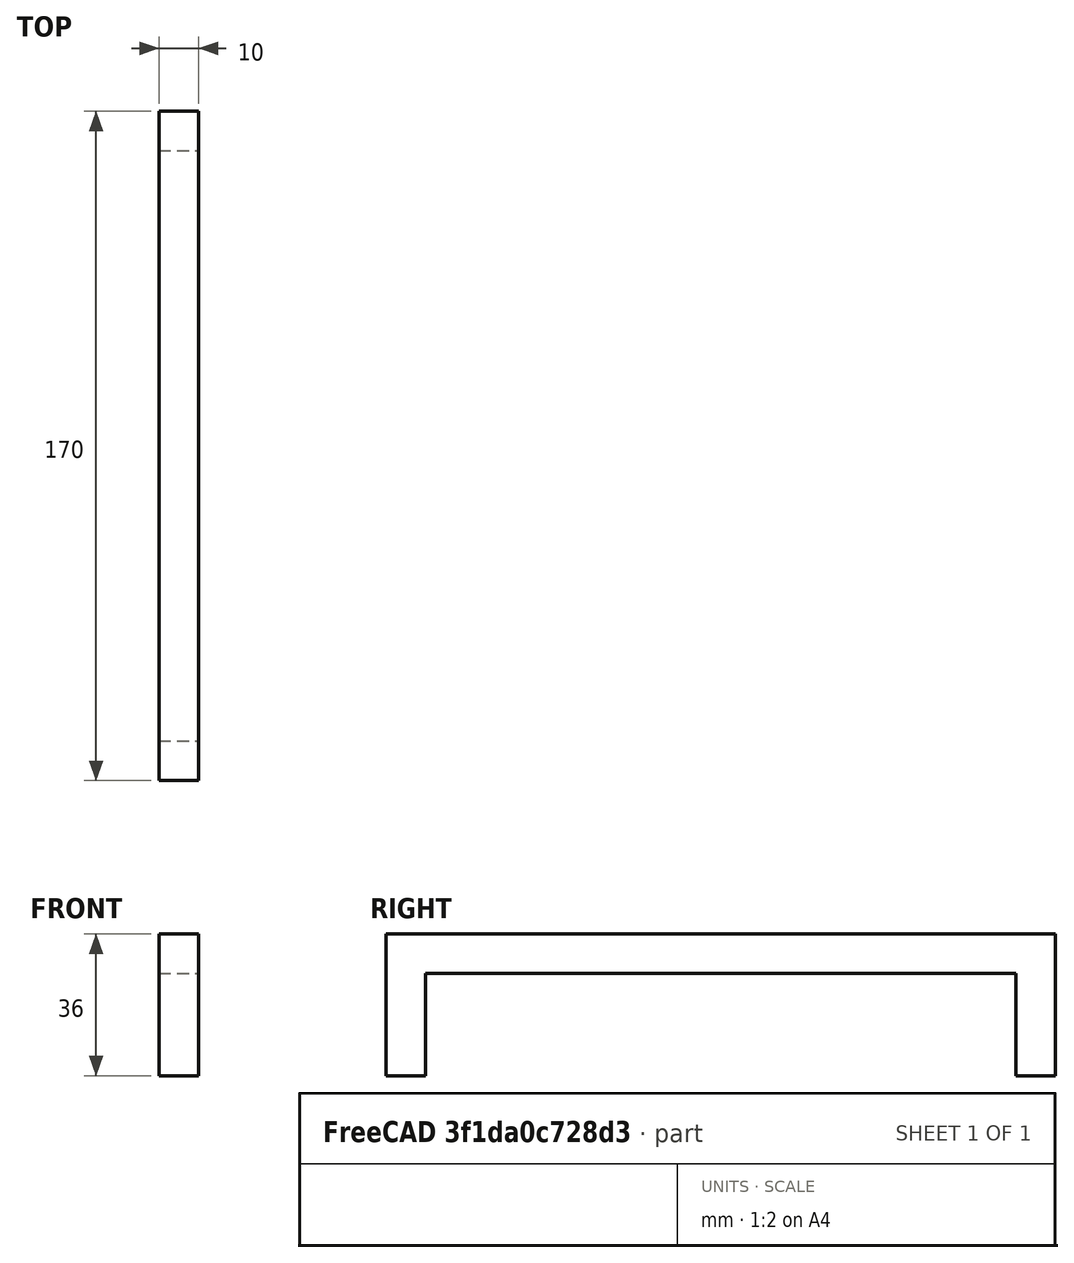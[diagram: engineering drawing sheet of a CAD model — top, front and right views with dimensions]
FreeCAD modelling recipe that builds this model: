
FCSTD DOCUMENT  (FreeCAD 1.1R20260325 (Git shallow))
Label: msf069
License: All rights reserved
LicenseURL: https://en.wikipedia.org/wiki/All_rights_reserved
objects: App::LinkGroup×2, App::Point×2, Sketcher::SketchObject×1, PartDesign::Pad×1, PartDesign::Body×1, App::Part×1
note: 6 computed .brp shape members not serialized (recipe doc carries the construction recipe); baked Part::Feature solids carry a one-line shape summary decoded from their .brp

FEATURE [Sketcher::SketchObject] Sketch
  ArcFitTolerance = 0
  ExternalTypes = [0]
  FullyConstrained = true
  MakeInternals = false
  MapMode = 5
  Placement = pos=(0,0,0) rot=(0.57735,0.57735,0.57735;2.0944rad)
  _ExternalGeoVersion = 0
  sketch-geometry (8):
    g0: LineSegment StartX=75 StartY=0 StartZ=0 EndX=85 EndY=0 EndZ=0
    g1: LineSegment StartX=85 StartY=0 StartZ=0 EndX=85 EndY=36 EndZ=0
    g2: LineSegment StartX=85 StartY=36 StartZ=0 EndX=-85 EndY=36 EndZ=0
    g3: LineSegment StartX=-85 StartY=36 StartZ=0 EndX=-85 EndY=0 EndZ=0
    g4: LineSegment StartX=-85 StartY=0 StartZ=0 EndX=-75 EndY=0 EndZ=0
    g5: LineSegment StartX=-75 StartY=0 StartZ=0 EndX=-75 EndY=26 EndZ=0
    g6: LineSegment StartX=-75 StartY=26 StartZ=0 EndX=75 EndY=26 EndZ=0
    g7: LineSegment StartX=75 StartY=26 StartZ=0 EndX=75 EndY=0 EndZ=0
  constraints (23):
    c: PointOnObject(g0,g-1)
    c: PointOnObject(g0,g-1)
    c: Coincident(g0,g1)
    c: Vertical(g1)
    c: Coincident(g1,g2)
    c: Horizontal(g2)
    c: Coincident(g2,g3)
    c: PointOnObject(g3,g-1)
    c: Vertical(g3)
    c: Coincident(g3,g4)
    c: Vertical(g5)
    c: Horizontal(g6)
    c: Coincident(g6,g7)
    c: Coincident(g7,g0)
    c: Vertical(g7)
    c: DistanceY(g6,g1) = 10
    c: DistanceX(g0,g0) = 10
    c: DistanceX(g3,g4) = 10
    c: DistanceX(g4,g0) = 150
    c: DistanceY(g3,g2) = 36
    c: Coincident(g5,g6)
    c: Coincident(g5,g4)
    c: Symmetric(g4,g0,g-1)
FEATURE [PartDesign::Pad] Pad
  Direction = (1,1e-16,-1e-16)
  Length = 10
  Length2 = 10
  Placement = pos=(0,0,0) rot=(0.57735,0.57735,0.57735;2.0944rad)
  Profile = -> Sketch
  ReferenceAxis = -> Sketch [N_Axis]
  SideType = 2
  Suppressed = false
  Type = 0
  Type2 = 0
FEATURE [PartDesign::Body] Body
  AllowCompound = true
  Group = -> [Sketch,Pad]
  Origin = -> Origin001
  Tip = -> Pad
FEATURE [App::Part] Part
  Group = -> [Body]
  Origin = -> Origin
FEATURE [App::LinkGroup] LinkGroup  label="Cabinet handle, link this"
  ElementList = -> [Part]
  LinkMode = 0
FEATURE [App::LinkGroup] LinkGroup001  label="Cabinet handle, hide this"
  ElementList = -> [LinkGroup]
  LinkMode = 0
FEATURE [App::Point] Origin002  label="Origin"
  Role = Origin
FEATURE [App::Point] Origin003  label="Origin"
  Role = Origin
